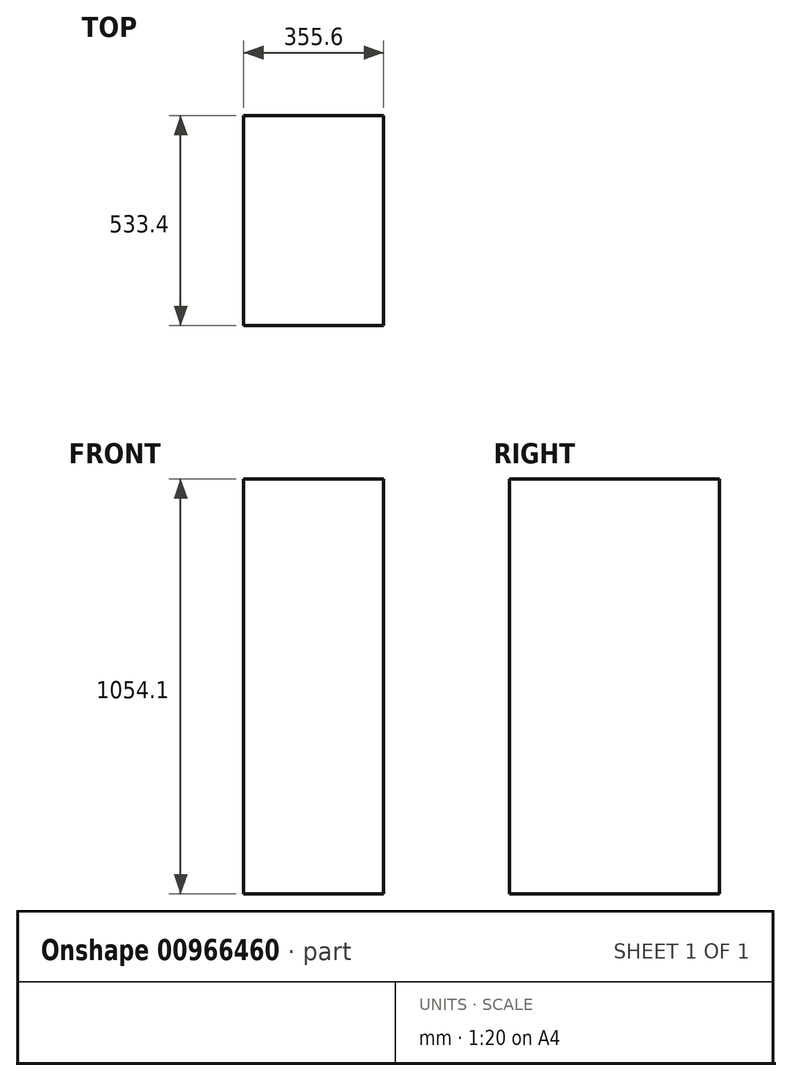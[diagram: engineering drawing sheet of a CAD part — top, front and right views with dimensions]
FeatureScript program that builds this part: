
annotation { "Feature Type Name" : "Feature", "Feature Type Description" : "" }
export const myFeature = defineFeature(function(context is Context, id is Id, definition is map)
    precondition{}
    {
        {
            var Q0;
            Q0=qCreatedBy(makeId("Top.planeOp"),FACE);
            var sketch = newSketch(context, id + "F0", { "sketchPlane" : qUnion([Q0])});
            skLineSegment(sketch, "E0.bottom", {"start": v(177.8, -266.7) * mm, "end": v(-177.8, -266.7) * mm});
            skLineSegment(sketch, "E0.top", {"start": v(177.8, 266.7) * mm, "end": v(-177.8, 266.7) * mm});
            skLineSegment(sketch, "E0.left", {"start": v(177.8, -266.7) * mm, "end": v(177.8, 266.7) * mm});
            skLineSegment(sketch, "E0.right", {"start": v(-177.8, -266.7) * mm, "end": v(-177.8, 266.7) * mm});
            skPoint(sketch, "E0.middle", {"position": v(0, 0) * mm});
            skSolve(sketch);
        }
        {
            var Q0;
            Q0 = qSketchRegion(id + "F0", true);
            extrude(context, id + "F1", {"entities" : qUnion([Q0]), "depth" : 1054.1 * mm, "offsetDistance" : 25.4 * mm});
        }
    });
